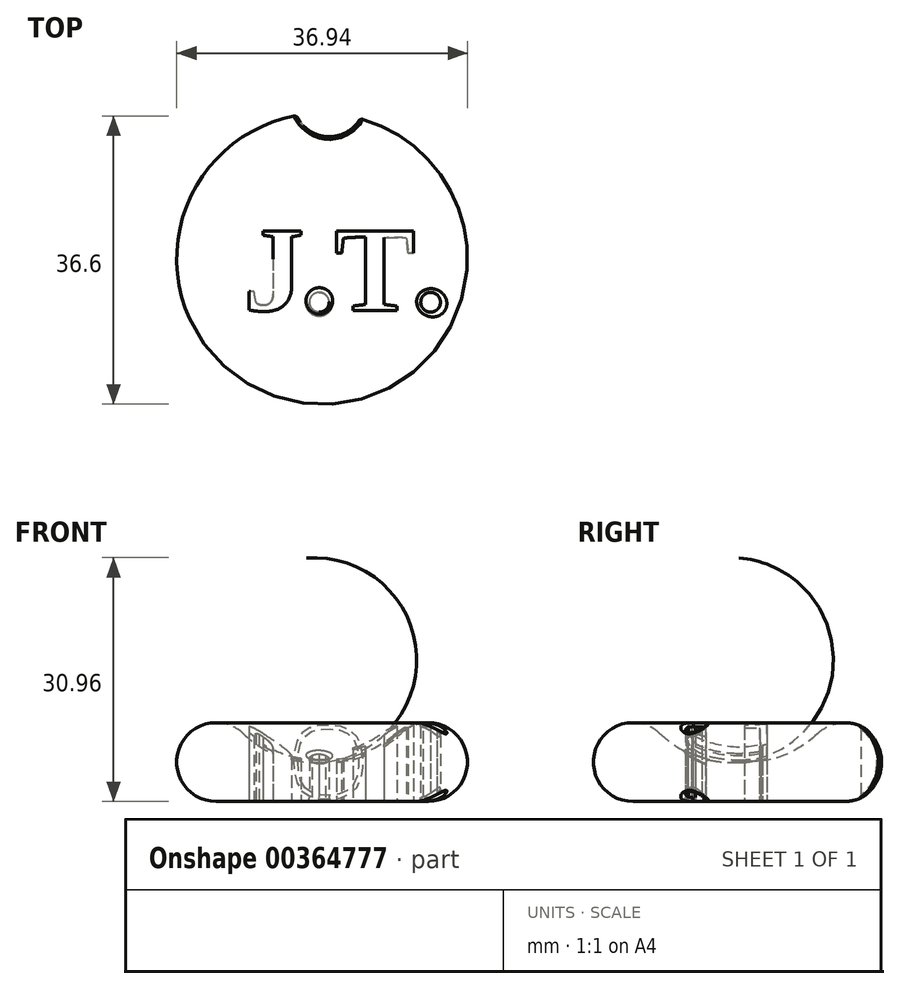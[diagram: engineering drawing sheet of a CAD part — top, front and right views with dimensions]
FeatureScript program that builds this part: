
annotation { "Feature Type Name" : "Feature", "Feature Type Description" : "" }
export const myFeature = defineFeature(function(context is Context, id is Id, definition is map)
    precondition{}
    {
        {
            var Q0;
            Q0=qCreatedBy(makeId("Front.planeOp"),FACE);
            var sketch = newSketch(context, id + "F0", { "sketchPlane" : qUnion([Q0])});
            skArc(sketch, "E0", {"start": v(-51.45, 8.6) * mm, "mid": v(-59.56, 6.87) * mm, "end": v(-54.92, 0) * mm});
            skArc(sketch, "E1", {"start": v(-51.45, 8.6) * mm, "mid": v(-46.83, 5.73) * mm, "end": v(-41.45, 5) * mm});
            skLineSegment(sketch, "E2", {"start": v(-55.33, 0) * mm, "end": v(-41.45, 0) * mm});
            skLineSegment(sketch, "E3", {"start": v(-41.45, 0) * mm, "end": v(-41.45, 5) * mm});
            skSolve(sketch);
        }
        {
            var Q0;
            {var subQ2=sQuery(id+"F0.wireOp",EDGE,"E0");Q0=makeQuery(id+"F0.imprint","IMPRINT",FACE,{"disambiguationData":[TD([[makeQuery(id+"F0.imprint","IMPRINT",EDGE,{"derivedFrom":subQ2}),1.0]])]});}
            var Q1;
            Q1=sQuery(id+"F0.wireOp",EDGE,"E3");
            revolve(context, id + "F1", {"entities" : qUnion([Q0]), "axis" : qUnion([Q1]), "revolveType" : RevolveType.FULL});
        }
        {
            var Q0;
            Q0=qCreatedBy(makeId("Top.planeOp"),FACE);
            cPlane(context, id + "F2", {"entities" : qUnion([Q0]), "cplaneType" : CPlaneType.OFFSET, "offset" : 9 * mm, "oppositeDirection" : true, "width" : 150 * mm, "height" : 150 * mm});
        }
        {
            var Q0;
            Q0=qCreatedBy(id+"F2.planeOp",FACE);
            var sketch = newSketch(context, id + "F3", { "sketchPlane" : qUnion([Q0])});
            skText(sketch, "E4", { "text": "J.T.", "fontName": "Tinos-Bold.ttf"});
            const initialGuessF3  = {"E4": [-0.05144, -0.00655, 1, 0, 0.0111]};
            skSetInitialGuess(sketch, initialGuessF3);
            skSolve(sketch);
        }
        {
            var Q0;
            Q0 = qSketchRegion(id + "F3", true);
            extrude(context, id + "F4", {"entities" : qUnion([Q0]), "operationType" : NewBodyOperationType.REMOVE, "endBound" : BoundingType.THROUGH_ALL, "depth" : 25 * mm});
        }
        {
            var Q0;
            Q0=qCreatedBy(id+"F2.planeOp",FACE);
            var sketch = newSketch(context, id + "F5", { "sketchPlane" : qUnion([Q0])});
            skCircle(sketch, "E5", {"center": v(-40.55, 20) * mm, "radius": 4.5 * mm});
            skSolve(sketch);
        }
        {
            var Q0;
            Q0=makeQuery(id+"F5.imprint","IMPRINT",FACE,{"disambiguationData":[TD([[makeQuery(id+"F5.imprint","IMPRINT",EDGE,{"derivedFrom":sQuery(id+"F5.wireOp",EDGE,"E5")}),1.0]])]});
            extrude(context, id + "F6", {"entities" : qUnion([Q0]), "operationType" : NewBodyOperationType.REMOVE, "endBound" : BoundingType.THROUGH_ALL, "depth" : 25 * mm});
        }
        {
            var Q0;
            Q0=makeQuery(id+"F6.boolean.opBoolean","INTERSECT",EDGE,{"derivedFrom":[makeQuery(id+"F4.boolean.opBoolean","SPLIT",FACE,{"disambiguationData":[TD([makeQuery(id+"F1.opRevolve","SWEPT_FACE",FACE,{"disambiguationData":[OSD([sQuery(id+"F0.wireOp",EDGE,"E2")])]})])],"derivedFrom":makeQuery(id+"F1.opRevolve","SWEPT_FACE",FACE,{"disambiguationData":[OSD([sQuery(id+"F0.wireOp",EDGE,"E0")])]})}),makeQuery(id+"F6.opExtrude","SWEPT_FACE",FACE,{"disambiguationData":[OSD([sQuery(id+"F5.wireOp",EDGE,"E5")])]})]});
            fillet(context, id + "F7", {"entities" : qUnion([Q0]), "radius" : .5 * mm, "tangentPropagation" : true, "allowEdgeOverflow" : false});
        }
        {
            var Q0;
            Q0=makeQuery(id+"F4.boolean.opBoolean","INTERSECT",EDGE,{"derivedFrom":[makeQuery(id+"F1.opRevolve","SWEPT_FACE",FACE,{"disambiguationData":[OSD([sQuery(id+"F0.wireOp",EDGE,"E1")])]}),makeQuery(id+"F4.opExtrude","SWEPT_FACE",FACE,{"disambiguationData":[OSD([sQuery(id+"F3.wireOp",EDGE,"E4.sketch_text.stroke-25")])]})]});
            var Q1;
            Q1=makeQuery(id+"F4.boolean.opBoolean","INTERSECT",EDGE,{"derivedFrom":[makeQuery(id+"F1.opRevolve","SWEPT_FACE",FACE,{"disambiguationData":[OSD([sQuery(id+"F0.wireOp",EDGE,"E1")])]}),makeQuery(id+"F4.opExtrude","SWEPT_FACE",FACE,{"disambiguationData":[OSD([sQuery(id+"F3.wireOp",EDGE,"E4.sketch_text.stroke-24")])]})]});
            var Q2;
            Q2=makeQuery(id+"F4.boolean.opBoolean","INTERSECT",EDGE,{"disambiguationData":[OD(1.0)],"derivedFrom":[makeQuery(id+"F1.opRevolve","SWEPT_FACE",FACE,{"disambiguationData":[OSD([sQuery(id+"F0.wireOp",EDGE,"E0")])]}),makeQuery(id+"F4.opExtrude","SWEPT_FACE",FACE,{"disambiguationData":[OSD([sQuery(id+"F3.wireOp",EDGE,"E4.sketch_text.stroke-47")])]})]});
            var Q3;
            Q3=makeQuery(id+"F4.boolean.opBoolean","INTERSECT",EDGE,{"disambiguationData":[OD(0.0)],"derivedFrom":[makeQuery(id+"F1.opRevolve","SWEPT_FACE",FACE,{"disambiguationData":[OSD([sQuery(id+"F0.wireOp",EDGE,"E0")])]}),makeQuery(id+"F4.opExtrude","SWEPT_FACE",FACE,{"disambiguationData":[OSD([sQuery(id+"F3.wireOp",EDGE,"E4.sketch_text.stroke-45")])]})]});
            var Q4;
            Q4=makeQuery(id+"F4.boolean.opBoolean","INTERSECT",EDGE,{"derivedFrom":[makeQuery(id+"F1.opRevolve","SWEPT_FACE",FACE,{"disambiguationData":[OSD([sQuery(id+"F0.wireOp",EDGE,"E2")])]}),makeQuery(id+"F4.opExtrude","SWEPT_FACE",FACE,{"disambiguationData":[OSD([sQuery(id+"F3.wireOp",EDGE,"E4.sketch_text.stroke-19")])]})]});
            fillet(context, id + "F8", {"entities" : qUnion([Q0, Q1, Q2, Q3, Q4]), "radius" : .5 * mm, "tangentPropagation" : true, "allowEdgeOverflow" : false});
        }
    });
